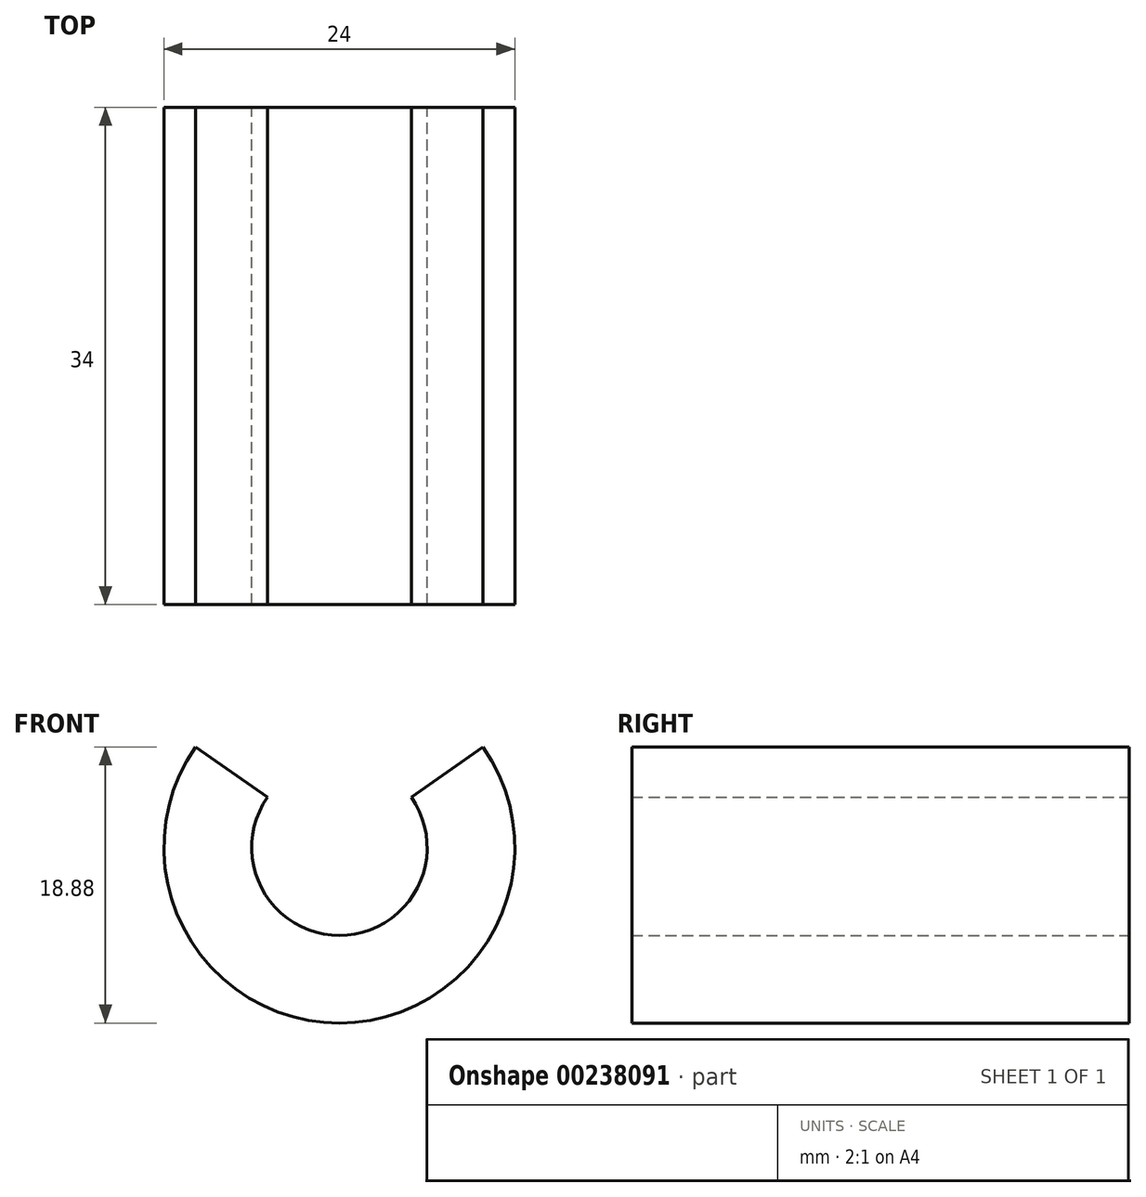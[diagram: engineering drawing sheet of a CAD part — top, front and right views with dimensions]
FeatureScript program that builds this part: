
annotation { "Feature Type Name" : "Feature", "Feature Type Description" : "" }
export const myFeature = defineFeature(function(context is Context, id is Id, definition is map)
    precondition{}
    {
        {
            var Q0;
            Q0=qCreatedBy(makeId("Front.planeOp"),FACE);
            var sketch = newSketch(context, id + "F0", { "sketchPlane" : qUnion([Q0])});
            skArc(sketch, "E0", {"start": v(-4.91, 3.44) * mm, "mid": v(0, -6) * mm, "end": v(4.91, 3.44) * mm});
            skArc(sketch, "E1", {"start": v(-9.83, 6.88) * mm, "mid": v(0, -12) * mm, "end": v(9.83, 6.88) * mm});
            skLineSegment(sketch, "E2", {"start": v(0, 0) * mm, "end": v(-9.83, 6.88) * mm});
            skLineSegment(sketch, "E3", {"start": v(0, 0) * mm, "end": v(9.83, 6.88) * mm});
            skPoint(sketch, "E4.left.start.orphan", {"position": v(-28.56, 20) * mm});
            skPoint(sketch, "E4.right.start.orphan", {"position": v(23.17, 16.22) * mm});
            skPoint(sketch, "E4.top.end.orphan", {"position": v(28.56, -20) * mm});
            skPoint(sketch, "E4.top.start.orphan", {"position": v(-23.17, -16.22) * mm});
            skSolve(sketch);
        }
        {
            var Q0;
            {var subQ0=sQuery(id+"F0.wireOp",EDGE,"E2");var subQ1=sQuery(id+"F0.wireOp",EDGE,"E0");var subQ2=makeQuery(id+"F0.imprint","INTERSECT",VERTEX,{"derivedFrom":[subQ1,subQ0]});Q0=makeQuery(id+"F0.imprint","IMPRINT",FACE,{"disambiguationData":[TD([[makeQuery(id+"F0.imprint","IMPRINT",EDGE,{"disambiguationData":[TD([[subQ2,-1.0]])],"derivedFrom":subQ1}),-1.0]])]});}
            extrude(context, id + "F1", {"entities" : qUnion([Q0]), "depth" : 34 * mm});
        }
    });
